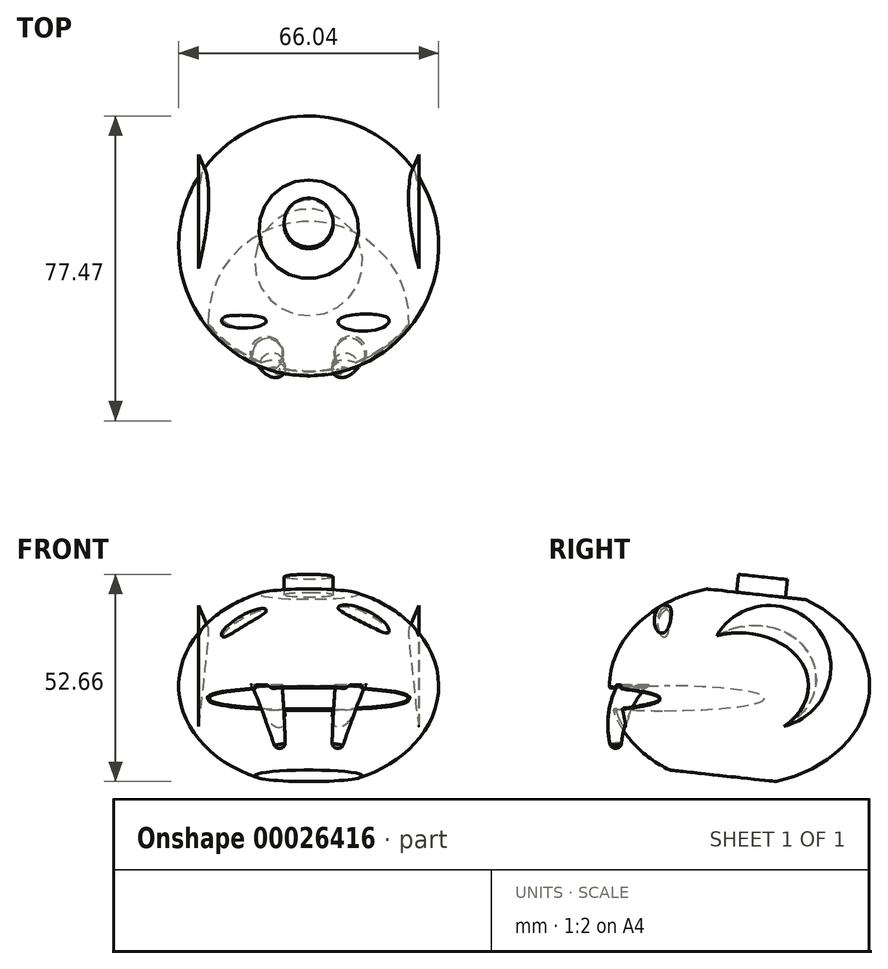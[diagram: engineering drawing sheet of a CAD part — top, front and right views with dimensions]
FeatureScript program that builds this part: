
annotation { "Feature Type Name" : "Feature", "Feature Type Description" : "" }
export const myFeature = defineFeature(function(context is Context, id is Id, definition is map)
    precondition{}
    {
        {
            var Q0;
            Q0=qCreatedBy(makeId("Front.planeOp"),FACE);
            var sketch = newSketch(context, id + "F0", { "sketchPlane" : qUnion([Q0])});
            skEllipse(sketch, "E0", {"center": v(0, 0) * mm, "majorRadius": 33.02 * mm, "minorRadius": 25.4 * mm, "majorAxis": v(1, 0)});
            skLineSegment(sketch, "E1", {"start": v(0, 25.4) * mm, "end": v(0, -25.4) * mm});
            skLineSegment(sketch, "E2", {"start": v(-33.02, 0) * mm, "end": v(33.02, 0) * mm, "construction": true});
            skSolve(sketch);
        }
        {
            var Q0;
            {var subQ0=sQuery(id+"F0.wireOp",EDGE,"E1");Q0=makeQuery(id+"F0.imprint","IMPRINT",FACE,{"disambiguationData":[TD([[makeQuery(id+"F0.imprint","IMPRINT",EDGE,{"derivedFrom":subQ0}),-1.0]])]});}
            var Q1;
            Q1=sQuery(id+"F0.wireOp",EDGE,"E1");
            revolve(context, id + "F1", {"entities" : qUnion([Q0]), "axis" : qUnion([Q1]), "revolveType" : RevolveType.FULL});
        }
        {
            var Q0;
            Q0=qCreatedBy(makeId("Front.planeOp"),FACE);
            cPlane(context, id + "F2", {"entities" : qUnion([Q0]), "cplaneType" : CPlaneType.OFFSET, "offset" : 19.05 * mm, "width" : 152.4 * mm, "height" : 152.4 * mm});
        }
        {
            var Q0;
            Q0=qCreatedBy(id+"F2.planeOp",FACE);
            var sketch = newSketch(context, id + "F3", { "sketchPlane" : qUnion([Q0])});
            skEllipse(sketch, "E3", {"center": v(13.85, 16.62) * mm, "majorRadius": 7.2 * mm, "minorRadius": 2.63 * mm, "majorAxis": v(0.9, -0.44)});
            skEllipse(sketch, "E4", {"center": v(-16.47, 16) * mm, "majorRadius": 6.52 * mm, "minorRadius": 1.84 * mm, "majorAxis": v(0.86, 0.5)});
            skLineSegment(sketch, "E5", {"start": v(7.39, 19.78) * mm, "end": v(20.32, 13.46) * mm});
            skLineSegment(sketch, "E6", {"start": v(-22.1, 12.7) * mm, "end": v(-10.84, 19.29) * mm});
            skSolve(sketch);
        }
        {
            var Q0;
            {var subQ0=sQuery(id+"F3.wireOp",EDGE,"E5");Q0=makeQuery(id+"F3.imprint","IMPRINT",FACE,{"disambiguationData":[TD([[makeQuery(id+"F3.imprint","IMPRINT",EDGE,{"derivedFrom":subQ0}),1.0]])]});}
            var Q1;
            Q1=sQuery(id+"F3.wireOp",EDGE,"E5");
            revolve(context, id + "F4", {"operationType" : NewBodyOperationType.ADD, "entities" : qUnion([Q0]), "axis" : qUnion([Q1]), "revolveType" : RevolveType.FULL});
        }
        {
            var Q0;
            {var subQ0=sQuery(id+"F3.wireOp",EDGE,"E6");Q0=makeQuery(id+"F3.imprint","IMPRINT",FACE,{"disambiguationData":[TD([[makeQuery(id+"F3.imprint","IMPRINT",EDGE,{"derivedFrom":subQ0}),1.0]])]});}
            var Q1;
            Q1=sQuery(id+"F3.wireOp",EDGE,"E6");
            revolve(context, id + "F5", {"operationType" : NewBodyOperationType.ADD, "entities" : qUnion([Q0]), "axis" : qUnion([Q1]), "revolveType" : RevolveType.FULL});
        }
        {
            var Q0;
            Q0=qCreatedBy(id+"F2.planeOp",FACE);
            var sketch = newSketch(context, id + "F6", { "sketchPlane" : qUnion([Q0])});
            skLineSegment(sketch, "E7", {"start": v(-25.4, -3.18) * mm, "end": v(25.4, -3.18) * mm, "construction": true});
            skLineSegment(sketch, "E8", {"start": v(0, -6.35) * mm, "end": v(0, 0) * mm});
            skEllipticalArc(sketch, "E9", {"construction": true});
            skEllipticalArc(sketch, "E10", {});
            skEllipticalArc(sketch, "E11", {"construction": true});
            const initialGuessF6  = {"E9": [0, -0.003175, 1, 0, 0.0254, 0.003175, 1.3491643344682913, 1.5707963267948966], "E10": [0, -0.003175, 1, 0, 0.0254, 0.003175, 1.5707963267948966, 4.71238898038469], "E11": [0, -0.003175, 1, 0, 0.0254, 0.003175, 4.71238898038469, 1.3491643344682913]};
            skSetInitialGuess(sketch, initialGuessF6);
            skSolve(sketch);
        }
        {
            var Q0;
            Q0=qSketchRegion(id+"F6",true);
            var Q1;
            Q1=sQuery(id+"F6.wireOp",EDGE,"E8");
            revolve(context, id + "F7", {"operationType" : NewBodyOperationType.REMOVE, "entities" : qUnion([Q0]), "axis" : qUnion([Q1]), "revolveType" : RevolveType.FULL, "oppositeDirection" : true});
        }
        {
            var Q0;
            Q0=qCreatedBy(makeId("Top.planeOp"),FACE);
            cPlane(context, id + "F8", {"entities" : qUnion([Q0]), "cplaneType" : CPlaneType.OFFSET, "offset" : 7.62 * mm, "oppositeDirection" : true, "width" : 152.4 * mm, "height" : 152.4 * mm});
        }
        {
            var Q0;
            Q0=qCreatedBy(id+"F8.planeOp",FACE);
            var sketch = newSketch(context, id + "F9", { "sketchPlane" : qUnion([Q0])});
            skCircle(sketch, "E12", {"center": v(11.74, -24.8) * mm, "radius": 3.81 * mm});
            skLineSegment(sketch, "E13", {"start": v(11.74, -24.8) * mm, "end": v(13.27, -8.97) * mm, "construction": true});
            skSolve(sketch);
        }
        {
            var Q0;
            Q0=sQuery(id+"F9.wireOp",EDGE,"E13");
            cPlane(context, id + "F10", {"entities" : qUnion([Q0]), "cplaneType" : CPlaneType.LINE_ANGLE, "offset" : 152.4 * mm, "angle" : 100 * degree, "width" : 152.4 * mm, "height" : 152.4 * mm});
        }
        {
            var Q0;
            Q0=qCreatedBy(id+"F10.planeOp",FACE);
            var sketch = newSketch(context, id + "F11", { "sketchPlane" : qUnion([Q0])});
            skArc(sketch, "E14", {"start": v(-36.17, 14.54) * mm, "mid": v(-33.36, 3.79) * mm, "end": v(-27.28, -5.52) * mm});
            skEllipse(sketch, "E15.0", {"center": v(-23.47, -5.46) * mm, "majorRadius": 3.81 * mm, "minorRadius": 1.3 * mm, "majorAxis": v(1, 0.02), "construction": true});
            skSolve(sketch);
        }
        {
            var Q0;
            Q0=sQuery(id+"F11.wireOp",VERTEX,"E14.start");
            var Q1;
            Q1=qCreatedBy(makeId("Top.planeOp"),FACE);
            cPlane(context, id + "F12", {"entities" : qUnion([Q0, Q1]), "cplaneType" : CPlaneType.PLANE_POINT, "offset" : 152.4 * mm, "width" : 152.4 * mm, "height" : 152.4 * mm});
        }
        {
            var Q0;
            Q0=qCreatedBy(id+"F12.planeOp",FACE);
            var sketch = newSketch(context, id + "F13", { "sketchPlane" : qUnion([Q0])});
            skCircle(sketch, "E16", {"center": v(14.04, -36.18) * mm, "radius": 1.27 * mm});
            skLineSegment(sketch, "E17", {"start": v(14.04, -36.18) * mm, "end": v(14.04, -40.28) * mm, "construction": true});
            skSolve(sketch);
        }
        {
            var Q0;
            Q0=qCreatedBy(makeId("Right.planeOp"),FACE);
            var sketch = newSketch(context, id + "F14", { "sketchPlane" : qUnion([Q0])});
            skLineSegment(sketch, "E18", {"start": v(-31.67, -19.92) * mm, "end": v(28.13, -26.36) * mm});
            skLineSegment(sketch, "E19", {"start": v(28.13, -26.36) * mm, "end": v(3.6, -39.68) * mm});
            skLineSegment(sketch, "E20", {"start": v(3.6, -39.68) * mm, "end": v(-29.81, -32.74) * mm});
            skLineSegment(sketch, "E21", {"start": v(-29.81, -32.74) * mm, "end": v(-31.67, -19.92) * mm});
            skLineSegment(sketch, "E22", {"start": v(-30.38, 26.96) * mm, "end": v(41.38, 19.23) * mm});
            skLineSegment(sketch, "E23", {"start": v(41.38, 19.23) * mm, "end": v(33.82, 34.28) * mm});
            skLineSegment(sketch, "E24", {"start": v(33.82, 34.28) * mm, "end": v(-14.03, 43.49) * mm});
            skLineSegment(sketch, "E25", {"start": v(-14.03, 43.49) * mm, "end": v(-30.38, 26.96) * mm});
            skSolve(sketch);
        }
        {
            var Q0;
            Q0=qSketchRegion(id+"F14",true);
            extrude(context, id + "F15", {"entities" : qUnion([Q0]), "operationType" : NewBodyOperationType.REMOVE, "endBound" : BoundingType.SYMMETRIC, "oppositeDirection" : true, "depth" : 101.6 * mm});
        }
        {
            var Q0;
            Q0=makeQuery(id+"F15.boolean.opBoolean","COPY",FACE,{"derivedFrom":makeQuery(id+"F15.opExtrude","SWEPT_FACE",FACE,{"disambiguationData":[OSD([sQuery(id+"F14.wireOp",EDGE,"E22")])]})});
            var sketch = newSketch(context, id + "F16", { "sketchPlane" : qUnion([Q0])});
            skCircle(sketch, "E26", {"center": v(0, 2.94) * mm, "radius": 6.22 * mm});
            skLineSegment(sketch, "E27", {"start": v(-12.6, 2.94) * mm, "end": v(12.6, 2.94) * mm, "construction": true});
            skLineSegment(sketch, "E28", {"start": v(0, 14.33) * mm, "end": v(0, -10.9) * mm, "construction": true});
            skSolve(sketch);
        }
        {
            var Q0;
            Q0=qSketchRegion(id+"F16",true);
            extrude(context, id + "F17", {"entities" : qUnion([Q0]), "operationType" : NewBodyOperationType.ADD, "depth" : 4.57 * mm});
        }
        {
            var Q0;
            Q0=makeQuery(id+"F7.boolean.opBoolean","INTERSECT",EDGE,{"derivedFrom":[makeQuery(id+"F1.opRevolve","SWEPT_FACE",FACE,{"disambiguationData":[OSD([sQuery(id+"F0.wireOp",EDGE,"E0")])]}),makeQuery(id+"F7.opRevolve","SWEPT_FACE",FACE,{"disambiguationData":[OSD([sQuery(id+"F6.wireOp",EDGE,"E10")])]})]});
            fillet(context, id + "F18", {"entities" : qUnion([Q0]), "radius" : 0.25 * mm, "tangentPropagation" : true, "allowEdgeOverflow" : false});
        }
        {
            var Q0;
            Q0=qCreatedBy(makeId("Top.planeOp"),FACE);
            var sketch = newSketch(context, id + "F19", { "sketchPlane" : qUnion([Q0])});
            skCircle(sketch, "E29", {"center": v(10.54, -27.32) * mm, "radius": 3.81 * mm});
            skLineSegment(sketch, "E30", {"start": v(10.54, -27.32) * mm, "end": v(12.51, -10.96) * mm, "construction": true});
            skSolve(sketch);
        }
        {
            var Q0;
            Q0=qCreatedBy(makeId("Top.planeOp"),FACE);
            cPlane(context, id + "F20", {"entities" : qUnion([Q0]), "cplaneType" : CPlaneType.OFFSET, "offset" : 15.88 * mm, "oppositeDirection" : true, "width" : 152.4 * mm, "height" : 152.4 * mm});
        }
        {
            var Q0;
            Q0=sQuery(id+"F19.wireOp",VERTEX,"E30.start");
            var Q1;
            Q1=qCreatedBy(id+"F10.planeOp",FACE);
            cPlane(context, id + "F21", {"entities" : qUnion([Q0, Q1]), "cplaneType" : CPlaneType.PLANE_POINT, "offset" : 152.4 * mm, "width" : 152.4 * mm, "height" : 152.4 * mm});
        }
        {
            var Q0;
            Q0=qCreatedBy(id+"F21.planeOp",FACE);
            var sketch = newSketch(context, id + "F22", { "sketchPlane" : qUnion([Q0])});
            skArc(sketch, "E31", {"start": v(-30.02, 1.78) * mm, "mid": v(-32.28, -6.16) * mm, "end": v(-31.53, -14.37) * mm});
            skSolve(sketch);
        }
        {
            var Q0;
            Q0=qCreatedBy(id+"F20.planeOp",FACE);
            var sketch = newSketch(context, id + "F23", { "sketchPlane" : qUnion([Q0])});
            skCircle(sketch, "E32", {"center": v(7.22, -31.35) * mm, "radius": 1.27 * mm});
            skLineSegment(sketch, "E33", {"start": v(7.22, -31.35) * mm, "end": v(7.22, -32.62) * mm, "construction": true});
            skSolve(sketch);
        }
        {
            var Q1;
            Q1 = qSketchRegion(id + "F23", true);
            var Q2;
            Q2 = qSketchRegion(id + "F19", true);
            var Q3;
            Q3 = qConstructionFilter(qBodyType(qCreatedBy(id + "F22" ,EDGE), BodyType.WIRE), ConstructionObject.NO);
            loft(context, id + "F24", {"addGuides" : true, "sheetProfilesArray" : [{ "sheetProfileEntities" : qUnion([Q1]) }, { "sheetProfileEntities" : qUnion([Q2]) }], "guidesArray" : [{ "guideEntities" : qUnion([Q3]), "guideDerivativeType" : LoftGuideDerivativeType.DEFAULT, "guideDerivativeMagnitude" : 1 }]});
        }
        {
            var Q0;
            Q0=makeQuery(id+"F24.opLoft","MID_CAP_EDGE",EDGE,{"disambiguationData":[OSD([sQuery(id+"F22.wireOp",EDGE,"E31"),sQuery(id+"F23.wireOp",EDGE,"E32")])],"capPos":0.0});
            fillet(context, id + "F25", {"entities" : qUnion([Q0]), "radius" : 1.27 * mm, "tangentPropagation" : true, "allowEdgeOverflow" : false});
        }
        {
            var Q0;
            Q0=makeQuery(id+"F24.opLoft","SWEPT_BODY",BODY,{"disambiguationData":[OSD([makeQuery(id+"F19.imprint","IMPRINT",FACE,{"disambiguationData":[TD([[makeQuery(id+"F19.imprint","IMPRINT",EDGE,{"derivedFrom":sQuery(id+"F19.wireOp",EDGE,"E29")}),1.0]])]}),sQuery(id+"F22.wireOp",EDGE,"E31"),makeQuery(id+"F23.imprint","IMPRINT",FACE,{"disambiguationData":[TD([[makeQuery(id+"F23.imprint","IMPRINT",EDGE,{"derivedFrom":sQuery(id+"F23.wireOp",EDGE,"E32")}),1.0]])]})])]});
            var Q1;
            Q1=qCreatedBy(makeId("Right.planeOp"),FACE);
            mirror(context, id + "F26", {"entities" : qUnion([Q0]), "mirrorPlane" : qUnion([Q1])});
        }
        {
            var Q0;
            Q0=makeQuery(id+"F26.opPattern","COPY",BODY,{"derivedFrom":makeQuery(id+"F24.opLoft","SWEPT_BODY",BODY,{"disambiguationData":[OSD([makeQuery(id+"F19.imprint","IMPRINT",FACE,{"disambiguationData":[TD([[makeQuery(id+"F19.imprint","IMPRINT",EDGE,{"derivedFrom":sQuery(id+"F19.wireOp",EDGE,"E29")}),1.0]])]}),sQuery(id+"F22.wireOp",EDGE,"E31"),makeQuery(id+"F23.imprint","IMPRINT",FACE,{"disambiguationData":[TD([[makeQuery(id+"F23.imprint","IMPRINT",EDGE,{"derivedFrom":sQuery(id+"F23.wireOp",EDGE,"E32")}),1.0]])]})])]}),"instanceName":"1"});
            var Q1;
            Q1=makeQuery(id+"F24.opLoft","SWEPT_BODY",BODY,{"disambiguationData":[OSD([makeQuery(id+"F19.imprint","IMPRINT",FACE,{"disambiguationData":[TD([[makeQuery(id+"F19.imprint","IMPRINT",EDGE,{"derivedFrom":sQuery(id+"F19.wireOp",EDGE,"E29")}),1.0]])]}),sQuery(id+"F22.wireOp",EDGE,"E31"),makeQuery(id+"F23.imprint","IMPRINT",FACE,{"disambiguationData":[TD([[makeQuery(id+"F23.imprint","IMPRINT",EDGE,{"derivedFrom":sQuery(id+"F23.wireOp",EDGE,"E32")}),1.0]])]})])]});
            var Q2;
            Q2=makeQuery(id+"F1.opRevolve","SWEPT_BODY",BODY,{"disambiguationData":[OSD([sQuery(id+"F0.wireOp",EDGE,"E0"),sQuery(id+"F0.wireOp",EDGE,"E1")])]});
            booleanBodies(context, id + "F27", {"operationType" : BooleanOperationType.SUBTRACTION, "tools" : qUnion([Q0, Q1]), "targets" : qUnion([Q2]), "offset" : true, "offsetAll" : true, "offsetDistance" : 0.25 * mm, "keepTools" : true});
        }
        {
            var Q0;
            Q0=qCreatedBy(makeId("Front.planeOp"),FACE);
            cPlane(context, id + "F28", {"entities" : qUnion([Q0]), "cplaneType" : CPlaneType.OFFSET, "offset" : 7.62 * mm, "oppositeDirection" : true, "width" : 152.4 * mm, "height" : 152.4 * mm});
        }
        {
            var Q0;
            Q0=qCreatedBy(id+"F28.planeOp",FACE);
            var sketch = newSketch(context, id + "F29", { "sketchPlane" : qUnion([Q0])});
            skLineSegment(sketch, "E34", {"start": v(28, 4.83) * mm, "end": v(28, 20.4) * mm});
            skLineSegment(sketch, "E35", {"start": v(28, 20.4) * mm, "end": v(21.18, 4.83) * mm});
            skLineSegment(sketch, "E36", {"start": v(21.18, 4.83) * mm, "end": v(28, 4.83) * mm});
            skSolve(sketch);
        }
        {
            var Q0;
            Q0 = qSketchRegion(id + "F29", true);
            var Q1;
            Q1=sQuery(id+"F29.wireOp",EDGE,"E36");
            revolve(context, id + "F30", {"entities" : qUnion([Q0]), "axis" : qUnion([Q1]), "revolveType" : RevolveType.FULL});
        }
        {
            var Q0;
            Q0=makeQuery(id+"F30.opRevolve","SWEPT_BODY",BODY,{"disambiguationData":[OSD([sQuery(id+"F29.wireOp",EDGE,"E34"),sQuery(id+"F29.wireOp",EDGE,"E35"),sQuery(id+"F29.wireOp",EDGE,"E36")])]});
            var Q1;
            Q1=qCreatedBy(makeId("Right.planeOp"),FACE);
            mirror(context, id + "F31", {"operationType" : NewBodyOperationType.ADD, "entities" : qUnion([Q0]), "mirrorPlane" : qUnion([Q1])});
        }
    });
